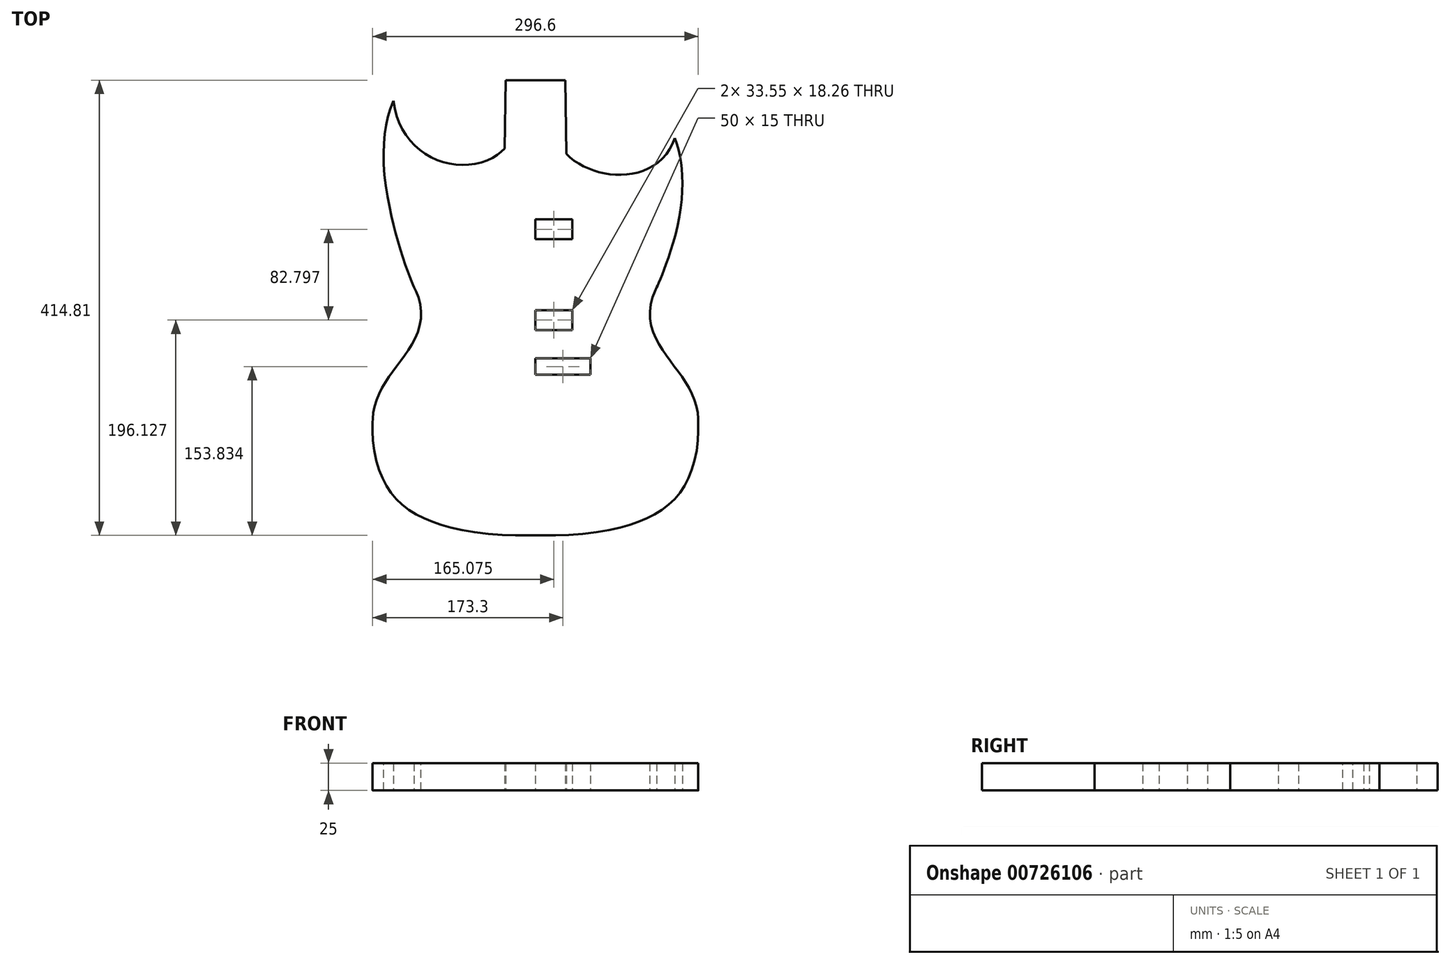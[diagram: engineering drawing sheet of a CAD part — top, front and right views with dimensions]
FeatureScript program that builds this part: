
annotation { "Feature Type Name" : "Feature", "Feature Type Description" : "" }
export const myFeature = defineFeature(function(context is Context, id is Id, definition is map)
    precondition{}
    {
        {
            var Q0;
            Q0=qCreatedBy(makeId("Top.planeOp"),FACE);
            var sketch = newSketch(context, id + "F0", { "sketchPlane" : qUnion([Q0])});
            skLineSegment(sketch, "E0", {"start": v(-27.25, 107.88) * mm, "end": v(27.25, 107.88) * mm});
            skLineSegment(sketch, "E1", {"start": v(27.25, 107.88) * mm, "end": v(28.25, 27.88) * mm});
            skLineSegment(sketch, "E2", {"start": v(28.25, 27.88) * mm, "end": v(-28.25, 27.88) * mm});
            skLineSegment(sketch, "E3", {"start": v(-28.25, 27.88) * mm, "end": v(-27.25, 107.88) * mm});
            skPoint(sketch, "E4", {"position": v(0, 107.88) * mm});
            skPoint(sketch, "E5", {"position": v(0, 27.88) * mm});
            skPoint(sketch, "E6", {"position": v(0, -113.44) * mm});
            skLineSegment(sketch, "E7", {"start": v(0, 140.47) * mm, "end": v(0, -316.9) * mm, "construction": true});
            skLineSegment(sketch, "E8", {"start": v(151.77, 125.26) * mm, "end": v(151.77, -318.22) * mm, "construction": true});
            skLineSegment(sketch, "E9", {"start": v(-118.71, 25.06) * mm, "end": v(-118.71, -316.9) * mm, "construction": true});
            skLineSegment(sketch, "E10", {"start": v(-118.71, -316.9) * mm, "end": v(151.77, -318.22) * mm, "construction": true});
            skFitSpline(sketch, "E11", {"points": [v(119.52, -85.17) * mm, v(118.71, 84.17) * mm], "startDerivative": vector(22.98, 48.55) * mm, "endDerivative": vector(-153.6, 152.06) * mm});
            skFitSpline(sketch, "E12", {"points": [v(27.81, 63) * mm, v(118.71, 84.17) * mm], "startDerivative": vector(14.52, -109.42) * mm, "endDerivative": vector(-23.51, 222.14) * mm});
            skLineSegment(sketch, "E13", {"start": v(-158.25, -204.45) * mm, "end": v(158.25, -204.45) * mm, "construction": true});
            skPoint(sketch, "E14", {"position": v(0, -204.45) * mm});
            skPoint(sketch, "E15", {"position": v(-118.71, 118.66) * mm});
            skFitSpline(sketch, "E16", {"points": [v(-119.52, -85.17) * mm, v(-118.71, 118.66) * mm], "startDerivative": vector(-24.03, 50.78) * mm, "endDerivative": vector(182.88, 149.62) * mm});
            skFitSpline(sketch, "E17", {"points": [v(-118.71, 118.66) * mm, v(-27.75, 67.88) * mm], "startDerivative": vector(-38.95, -275.92) * mm, "endDerivative": vector(18.07, 126.85) * mm});
            skFitSpline(sketch, "E18", {"points": [v(-158.25, -204.45) * mm, v(0, -316.9) * mm], "startDerivative": vector(0, -257.3) * mm, "endDerivative": vector(320.22, 0) * mm});
            skFitSpline(sketch, "E19", {"points": [v(-158.25, -204.45) * mm, v(-119.52, -85.17) * mm], "startDerivative": vector(1.82, 170.22) * mm, "endDerivative": vector(-67.84, 141.05) * mm});
            skFitSpline(sketch, "E20.MirrorCS", {"points": [v(158.25, -204.45) * mm, v(0, -316.9) * mm], "startDerivative": vector(0, -257.3) * mm, "endDerivative": vector(-320.22, 0) * mm});
            skFitSpline(sketch, "E21.MirrorCS", {"points": [v(158.25, -204.45) * mm, v(119.52, -85.17) * mm], "startDerivative": vector(-1.82, 170.22) * mm, "endDerivative": vector(67.84, 141.05) * mm});
            skLineSegment(sketch, "E22.MirrorCS", {"start": v(118.71, 25.06) * mm, "end": v(118.71, -316.9) * mm, "construction": true});
            skFitSpline(sketch, "E23.0", {"points": [v(-110.49, -80.9) * mm, v(-110.68, -80.48) * mm, v(-111.2, -79.35) * mm, v(-112.23, -76.92) * mm, v(-113.48, -73.83) * mm, v(-115.4, -68.91) * mm, v(-118.15, -61.38) * mm, v(-121.8, -50.44) * mm, v(-125.56, -37.94) * mm, v(-129.2, -24.18) * mm, v(-132.5, -9.48) * mm, v(-136.14, 10.93) * mm, v(-138.17, 31.92) * mm, v(-137.78, 52.15) * mm, v(-136.1, 66.58) * mm, v(-132.86, 79.96) * mm, v(-127.98, 91.97) * mm, v(-121.34, 102.4) * mm, v(-115.62, 108.27) * mm, v(-112.38, 110.92) * mm]});
            skFitSpline(sketch, "E24.0", {"points": [v(-148.25, -204.56) * mm, v(-148.22, -201.45) * mm, v(-147.74, -195.59) * mm, v(-146, -187.57) * mm, v(-143.4, -180.15) * mm, v(-140.04, -173.14) * mm, v(-136.08, -166.44) * mm, v(-131.65, -159.93) * mm, v(-126.94, -153.53) * mm, v(-122.12, -147.12) * mm, v(-117.39, -140.58) * mm, v(-112.96, -133.75) * mm, v(-109.1, -126.45) * mm, v(-106.11, -118.5) * mm, v(-104.41, -109.83) * mm, v(-104.4, -100.54) * mm, v(-106.3, -90.86) * mm, v(-108.89, -84.22) * mm, v(-110.51, -80.84) * mm]});
            skFitSpline(sketch, "E25.0", {"points": [v(-148.25, -204.45) * mm, v(-148.25, -214.67) * mm, v(-147.1, -228.48) * mm, v(-143.39, -244.02) * mm, v(-139.57, -254.33) * mm, v(-134.74, -263.41) * mm, v(-128.89, -271.4) * mm, v(-121.95, -278.44) * mm, v(-113.84, -284.64) * mm, v(-104.45, -290.05) * mm, v(-93.71, -294.7) * mm, v(-81.6, -298.58) * mm, v(-63.58, -302.75) * mm, v(-37.6, -306.09) * mm, v(-13.13, -306.9) * mm, v(0, -306.9) * mm]});
            skFitSpline(sketch, "E26.0", {"points": [v(148.25, -204.45) * mm, v(148.25, -214.67) * mm, v(147.1, -228.48) * mm, v(143.39, -244.02) * mm, v(139.57, -254.33) * mm, v(134.74, -263.41) * mm, v(128.89, -271.4) * mm, v(121.95, -278.44) * mm, v(113.84, -284.64) * mm, v(104.45, -290.05) * mm, v(93.71, -294.7) * mm, v(81.6, -298.58) * mm, v(63.58, -302.75) * mm, v(37.6, -306.09) * mm, v(13.13, -306.9) * mm, v(0, -306.9) * mm]});
            skFitSpline(sketch, "E27.0", {"points": [v(148.25, -204.56) * mm, v(148.22, -201.45) * mm, v(147.74, -195.59) * mm, v(146, -187.57) * mm, v(143.4, -180.15) * mm, v(140.04, -173.14) * mm, v(136.08, -166.44) * mm, v(131.65, -159.93) * mm, v(126.94, -153.53) * mm, v(122.12, -147.12) * mm, v(117.39, -140.58) * mm, v(112.96, -133.75) * mm, v(109.1, -126.45) * mm, v(106.11, -118.5) * mm, v(104.41, -109.83) * mm, v(104.4, -100.54) * mm, v(106.3, -90.86) * mm, v(108.89, -84.22) * mm, v(110.51, -80.84) * mm]});
            skFitSpline(sketch, "E28.0", {"points": [v(110.49, -80.9) * mm, v(110.7, -80.44) * mm, v(111.2, -79.36) * mm, v(112.46, -76.53) * mm, v(114.45, -71.84) * mm, v(117.27, -64.62) * mm, v(121.37, -53.14) * mm, v(126.66, -35.85) * mm, v(131.76, -12.12) * mm, v(133.76, 8.67) * mm, v(133.35, 25.02) * mm, v(131.89, 36.91) * mm, v(129.15, 48.23) * mm, v(125.01, 58.8) * mm, v(119.36, 68.48) * mm, v(114.45, 74.3) * mm, v(111.68, 77.06) * mm]});
            skPoint(sketch, "E29", {"position": v(-129, 89) * mm});
            skPoint(sketch, "E30", {"position": v(126.32, 55.19) * mm});
            skPoint(sketch, "E31", {"position": v(28.1, 39.62) * mm});
            skPoint(sketch, "E32", {"position": v(-28.03, 45.76) * mm});
            skFitSpline(sketch, "E33", {"points": [v(-128.62, 120.06) * mm, v(-129.49, 113.88) * mm, v(-130.32, 102.15) * mm, v(-129.04, 86.4) * mm, v(-125.41, 72.48) * mm, v(-119.7, 60.48) * mm, v(-112.18, 50.5) * mm, v(-103.3, 42.6) * mm, v(-93.45, 36.8) * mm, v(-83.04, 32.97) * mm, v(-72.43, 31.02) * mm, v(-61.89, 30.85) * mm, v(-51.69, 32.4) * mm, v(-42.09, 35.63) * mm, v(-34.84, 39.77) * mm, v(-29.67, 44) * mm, v(-26.2, 47.63) * mm, v(-23.17, 51.73) * mm, v(-20.7, 56.26) * mm, v(-18.86, 61.18) * mm, v(-18.1, 64.68) * mm, v(-17.85, 66.47) * mm]});
            skFitSpline(sketch, "E34", {"points": [v(17.68, 61.65) * mm, v(17.9, 59.98) * mm, v(18.6, 56.73) * mm, v(20.3, 52.14) * mm, v(22.59, 47.88) * mm, v(26.28, 42.67) * mm, v(31.9, 37.02) * mm, v(39.82, 31.49) * mm, v(48.65, 27.16) * mm, v(58.15, 24.03) * mm, v(68.1, 22.16) * mm, v(78.28, 21.66) * mm, v(88.48, 22.68) * mm, v(98.45, 25.44) * mm, v(107.87, 30.19) * mm, v(116.24, 37.13) * mm, v(122.95, 46.3) * mm, v(127.5, 57.47) * mm, v(129.65, 70.38) * mm, v(129.43, 80.1) * mm, v(128.88, 85.24) * mm]});
            skFitSpline(sketch, "E35", {"points": [v(17.68, 61.65) * mm, v(17.9, 59.98) * mm, v(18.6, 56.73) * mm, v(20.3, 52.14) * mm, v(22.59, 47.88) * mm, v(26.28, 42.67) * mm, v(31.9, 37.02) * mm, v(39.82, 31.49) * mm, v(48.65, 27.16) * mm, v(58.15, 24.03) * mm, v(68.1, 22.16) * mm, v(78.28, 21.66) * mm, v(88.48, 22.68) * mm, v(98.45, 25.44) * mm, v(107.87, 30.19) * mm, v(116.24, 37.13) * mm, v(122.95, 46.3) * mm, v(127.5, 57.47) * mm, v(129.65, 70.38) * mm, v(129.43, 80.1) * mm, v(128.88, 85.24) * mm]});
            skLineSegment(sketch, "E36.bottom", {"start": v(0, -101.67) * mm, "end": v(33.55, -101.67) * mm});
            skLineSegment(sketch, "E36.top", {"start": v(0, -119.93) * mm, "end": v(33.55, -119.93) * mm});
            skLineSegment(sketch, "E36.left", {"start": v(0, -101.67) * mm, "end": v(0, -119.93) * mm});
            skLineSegment(sketch, "E36.right", {"start": v(33.55, -101.67) * mm, "end": v(33.55, -119.93) * mm});
            skLineSegment(sketch, "E37.bottom", {"start": v(0, -145.6) * mm, "end": v(50, -145.6) * mm});
            skLineSegment(sketch, "E37.top", {"start": v(0, -160.6) * mm, "end": v(50, -160.6) * mm});
            skLineSegment(sketch, "E37.left", {"start": v(0, -145.6) * mm, "end": v(0, -160.6) * mm});
            skLineSegment(sketch, "E37.right", {"start": v(50, -145.6) * mm, "end": v(50, -160.6) * mm});
            skLineSegment(sketch, "E38", {"start": v(66.51, -153.1) * mm, "end": v(-64.3, -153.1) * mm, "construction": true});
            skPoint(sketch, "E38.startSnap0", {"position": v(50, -153.1) * mm});
            skLineSegment(sketch, "E39.bottom", {"start": v(0, -18.87) * mm, "end": v(33.55, -18.87) * mm});
            skLineSegment(sketch, "E39.top", {"start": v(0, -37.14) * mm, "end": v(33.55, -37.14) * mm});
            skLineSegment(sketch, "E39.left", {"start": v(0, -18.87) * mm, "end": v(0, -37.14) * mm});
            skLineSegment(sketch, "E39.right", {"start": v(33.55, -18.87) * mm, "end": v(33.55, -37.14) * mm});
            skLineSegment(sketch, "E40.MirrorCS", {"start": v(33.55, -287.32) * mm, "end": v(33.55, -269.06) * mm});
            skLineSegment(sketch, "E41.MirrorCS", {"start": v(0, -269.06) * mm, "end": v(33.55, -269.06) * mm});
            skLineSegment(sketch, "E42.MirrorCS", {"start": v(0, -287.32) * mm, "end": v(33.55, -287.32) * mm});
            skLineSegment(sketch, "E43.MirrorCS", {"start": v(33.55, -204.52) * mm, "end": v(33.55, -186.26) * mm});
            skLineSegment(sketch, "E44.MirrorCS", {"start": v(0, -186.26) * mm, "end": v(33.55, -186.26) * mm});
            skPoint(sketch, "E45.MirrorP", {"position": v(0, -192.75) * mm});
            skLineSegment(sketch, "E46.MirrorCS", {"start": v(0, -204.52) * mm, "end": v(33.55, -204.52) * mm});
            skLineSegment(sketch, "E47.MirrorCS", {"start": v(50, -160.6) * mm, "end": v(50, -145.6) * mm});
            skFitSpline(sketch, "E48", {"points": [v(55, -89.05) * mm, v(27.31, -101.67) * mm], "startDerivative": vector(-27.69, -12.62) * mm, "endDerivative": vector(-27.69, -12.62) * mm});
            skLineSegment(sketch, "E49", {"start": v(55.7, -18.3) * mm, "end": v(56.13, -17.15) * mm});
            skSolve(sketch);
        }
        {
            var Q0;
            {var subQ0=sQuery(id+"F0.wireOp",EDGE,"E3");var subQ1=sQuery(id+"F0.wireOp",EDGE,"E0");var subQ2=makeQuery(id+"F0.imprint","INTERSECT",VERTEX,{"derivedFrom":[subQ1,subQ0]});Q0=makeQuery(id+"F0.imprint","IMPRINT",FACE,{"disambiguationData":[TD([[makeQuery(id+"F0.imprint","IMPRINT",EDGE,{"disambiguationData":[TD([[subQ2,-1.0]])],"derivedFrom":subQ1}),-1.0]])]});}
            var Q1;
            {var subQ0=sQuery(id+"F0.wireOp",EDGE,"9AyLVo4j-rSeK-3mxc-JPnm-vFHV7DOMUlhE");var subQ1=sQuery(id+"F0.wireOp",EDGE,"E0");var subQ2=makeQuery(id+"F0.imprint","INTERSECT",VERTEX,{"disambiguationData":[OD(0.0)],"derivedFrom":[subQ1,subQ0]});Q1=makeQuery(id+"F0.imprint","IMPRINT",FACE,{"disambiguationData":[TD([[makeQuery(id+"F0.imprint","IMPRINT",EDGE,{"disambiguationData":[TD([[subQ2,-1.0]])],"derivedFrom":subQ1}),1.0]])]});}
            var Q2;
            {var subQ0=sQuery(id+"F0.wireOp",EDGE,"E1");var subQ1=sQuery(id+"F0.wireOp",EDGE,"E0");var subQ2=makeQuery(id+"F0.imprint","INTERSECT",VERTEX,{"derivedFrom":[subQ1,subQ0]});Q2=makeQuery(id+"F0.imprint","IMPRINT",FACE,{"disambiguationData":[TD([[makeQuery(id+"F0.imprint","IMPRINT",EDGE,{"disambiguationData":[TD([[subQ2,1.0]])],"derivedFrom":subQ1}),-1.0]])]});}
            var Q3;
            {var subQ0=sQuery(id+"F0.wireOp",EDGE,"8e891ce0-4720-4009-86df-1275f8929a3f");var subQ1=sQuery(id+"F0.wireOp",EDGE,"cQmTFEYe-NuiO-gJRc-wVYQ-j3BDNANN4NQr");var subQ2=makeQuery(id+"F0.imprint","INTERSECT",VERTEX,{"disambiguationData":[OD(0.0)],"derivedFrom":[subQ1,subQ0]});Q3=makeQuery(id+"F0.imprint","IMPRINT",FACE,{"disambiguationData":[TD([[makeQuery(id+"F0.imprint","IMPRINT",EDGE,{"disambiguationData":[TD([[subQ2,-1.0]])],"derivedFrom":subQ1}),1.0]])]});}
            var Q4;
            {var subQ0=sQuery(id+"F0.wireOp",EDGE,"6fe22ba0-2728-4f85-a325-eb2c5a9ddd98");var subQ1=sQuery(id+"F0.wireOp",EDGE,"cQmTFEYe-NuiO-gJRc-wVYQ-j3BDNANN4NQr");var subQ2=makeQuery(id+"F0.imprint","INTERSECT",VERTEX,{"disambiguationData":[OD(0.0)],"derivedFrom":[subQ1,subQ0]});Q4=makeQuery(id+"F0.imprint","IMPRINT",FACE,{"disambiguationData":[TD([[makeQuery(id+"F0.imprint","IMPRINT",EDGE,{"disambiguationData":[TD([[subQ2,1.0]])],"derivedFrom":subQ1}),1.0]])]});}
            var Q5;
            {var subQ0=sQuery(id+"F0.wireOp",EDGE,"6fe22ba0-2728-4f85-a325-eb2c5a9ddd98");var subQ1=sQuery(id+"F0.wireOp",EDGE,"9AyLVo4j-rSeK-3mxc-JPnm-vFHV7DOMUlhE");var subQ2=makeQuery(id+"F0.imprint","INTERSECT",VERTEX,{"disambiguationData":[OD(0.0)],"derivedFrom":[subQ1,subQ0]});Q5=makeQuery(id+"F0.imprint","IMPRINT",FACE,{"disambiguationData":[TD([[makeQuery(id+"F0.imprint","IMPRINT",EDGE,{"disambiguationData":[TD([[subQ2,-1.0]])],"derivedFrom":subQ1}),1.0]])]});}
            var Q6;
            {var subQ0=sQuery(id+"F0.wireOp",EDGE,"8e891ce0-4720-4009-86df-1275f8929a3f");var subQ1=sQuery(id+"F0.wireOp",EDGE,"9AyLVo4j-rSeK-3mxc-JPnm-vFHV7DOMUlhE");var subQ2=makeQuery(id+"F0.imprint","INTERSECT",VERTEX,{"disambiguationData":[OD(0.0)],"derivedFrom":[subQ1,subQ0]});Q6=makeQuery(id+"F0.imprint","IMPRINT",FACE,{"disambiguationData":[TD([[makeQuery(id+"F0.imprint","IMPRINT",EDGE,{"disambiguationData":[TD([[subQ2,1.0]])],"derivedFrom":subQ1}),1.0]])]});}
            var Q7;
            {var subQ0=sQuery(id+"F0.wireOp",EDGE,"8e891ce0-4720-4009-86df-1275f8929a3f");var subQ1=sQuery(id+"F0.wireOp",EDGE,"cQmTFEYe-NuiO-gJRc-wVYQ-j3BDNANN4NQr");var subQ2=makeQuery(id+"F0.imprint","INTERSECT",VERTEX,{"disambiguationData":[OD(1.0)],"derivedFrom":[subQ1,subQ0]});Q7=makeQuery(id+"F0.imprint","IMPRINT",FACE,{"disambiguationData":[TD([[makeQuery(id+"F0.imprint","IMPRINT",EDGE,{"disambiguationData":[TD([[subQ2,-1.0]])],"derivedFrom":subQ1}),-1.0]])]});}
            var Q8;
            {var subQ0=sQuery(id+"F0.wireOp",EDGE,"6fe22ba0-2728-4f85-a325-eb2c5a9ddd98");var subQ1=sQuery(id+"F0.wireOp",EDGE,"cQmTFEYe-NuiO-gJRc-wVYQ-j3BDNANN4NQr");var subQ2=makeQuery(id+"F0.imprint","INTERSECT",VERTEX,{"disambiguationData":[OD(1.0)],"derivedFrom":[subQ1,subQ0]});Q8=makeQuery(id+"F0.imprint","IMPRINT",FACE,{"disambiguationData":[TD([[makeQuery(id+"F0.imprint","IMPRINT",EDGE,{"disambiguationData":[TD([[subQ2,1.0]])],"derivedFrom":subQ1}),-1.0]])]});}
            var Q9;
            {var subQ0=sQuery(id+"F0.wireOp",EDGE,"6fe22ba0-2728-4f85-a325-eb2c5a9ddd98");var subQ1=sQuery(id+"F0.wireOp",EDGE,"cQmTFEYe-NuiO-gJRc-wVYQ-j3BDNANN4NQr");var subQ8=makeQuery(id+"F0.imprint","INTERSECT",VERTEX,{"disambiguationData":[OD(0.0)],"derivedFrom":[subQ1,subQ0]});Q9=makeQuery(id+"F0.imprint","IMPRINT",FACE,{"disambiguationData":[TD([[makeQuery(id+"F0.imprint","IMPRINT",EDGE,{"disambiguationData":[TD([[subQ8,-1.0]])],"derivedFrom":subQ1}),1.0]])]});}
            var Q10;
            {var subQ0=sQuery(id+"F0.wireOp",EDGE,"E2");Q10=makeQuery(id+"F0.imprint","IMPRINT",FACE,{"disambiguationData":[TD([[makeQuery(id+"F0.imprint","IMPRINT",EDGE,{"derivedFrom":subQ0}),-1.0]])]});}
            var Q11;
            {var subQ8=sQuery(id+"F0.wireOp",EDGE,"E2");Q11=makeQuery(id+"F0.imprint","IMPRINT",FACE,{"disambiguationData":[TD([[makeQuery(id+"F0.imprint","IMPRINT",EDGE,{"derivedFrom":subQ8}),1.0]])]});}
            var Q12;
            {var subQ0=sQuery(id+"F0.wireOp",EDGE,"9AyLVo4j-rSeK-3mxc-JPnm-vFHV7DOMUlhE");var subQ1=sQuery(id+"F0.wireOp",EDGE,"cQmTFEYe-NuiO-gJRc-wVYQ-j3BDNANN4NQr");var subQ2=makeQuery(id+"F0.imprint","INTERSECT",VERTEX,{"disambiguationData":[OD(0.0)],"derivedFrom":[subQ1,subQ0]});Q12=makeQuery(id+"F0.imprint","IMPRINT",FACE,{"disambiguationData":[TD([[makeQuery(id+"F0.imprint","IMPRINT",EDGE,{"disambiguationData":[TD([[subQ2,-1.0]])],"derivedFrom":subQ1}),1.0]])]});}
            var Q13;
            {var subQ1=sQuery(id+"F0.wireOp",EDGE,"cQmTFEYe-NuiO-gJRc-wVYQ-j3BDNANN4NQr");var subQ3=sQuery(id+"F0.wireOp",EDGE,"6a273922-8d34-43bc-820b-847c9d56296a");var subQ9=makeQuery(id+"F0.imprint","INTERSECT",VERTEX,{"disambiguationData":[OD(1.0)],"derivedFrom":[subQ1,subQ3]});Q13=makeQuery(id+"F0.imprint","IMPRINT",FACE,{"disambiguationData":[TD([[makeQuery(id+"F0.imprint","IMPRINT",EDGE,{"disambiguationData":[TD([[subQ9,-1.0]])],"derivedFrom":subQ1}),1.0]])]});}
            var Q14;
            {var subQ0=sQuery(id+"F0.wireOp",EDGE,"716289ee-55fe-485b-8154-cd30e735f9b1");var subQ1=sQuery(id+"F0.wireOp",EDGE,"cQmTFEYe-NuiO-gJRc-wVYQ-j3BDNANN4NQr");var subQ2=makeQuery(id+"F0.imprint","INTERSECT",VERTEX,{"disambiguationData":[OD(1.0)],"derivedFrom":[subQ1,subQ0]});Q14=makeQuery(id+"F0.imprint","IMPRINT",FACE,{"disambiguationData":[TD([[makeQuery(id+"F0.imprint","IMPRINT",EDGE,{"disambiguationData":[TD([[subQ2,1.0]])],"derivedFrom":subQ1}),-1.0]])]});}
            var Q15;
            {var subQ0=sQuery(id+"F0.wireOp",EDGE,"6a273922-8d34-43bc-820b-847c9d56296a");var subQ1=sQuery(id+"F0.wireOp",EDGE,"cQmTFEYe-NuiO-gJRc-wVYQ-j3BDNANN4NQr");var subQ2=makeQuery(id+"F0.imprint","INTERSECT",VERTEX,{"disambiguationData":[OD(1.0)],"derivedFrom":[subQ1,subQ0]});Q15=makeQuery(id+"F0.imprint","IMPRINT",FACE,{"disambiguationData":[TD([[makeQuery(id+"F0.imprint","IMPRINT",EDGE,{"disambiguationData":[TD([[subQ2,-1.0]])],"derivedFrom":subQ1}),-1.0]])]});}
            extrude(context, id + "F1", {"entities" : qUnion([Q0, Q1, Q2, Q3, Q4, Q5, Q6, Q7, Q8, Q9, Q10, Q11, Q12, Q13, Q14, Q15]), "depth" : 25 * mm, "offsetDistance" : 25 * mm});
        }
    });
